# Revit family: 0039273 Feilo Sylvania Lighting Fixtures SYLBAY LED 4000K 18-5KLM WIDE 1-10V PIR
name_source: partatom
category: Lighting Fixtures
revit_build: Autodesk Revit 2017 (Build: 20190507_1515(x64)
units: mm (PartAtom-declared; Revit-internal decimal feet)

## family parameters
Cut with Voids When Loaded = No
Host = Face
Light Source = Yes
OmniClass Number = 23.80.70.00
OmniClass Title = Lighting
Part Type = Normal
Room Calculation Point = No
Round Connector Dimension = Use Diameter
Shared = No

## types (1)
- 0039273 SYLBAY LED 4000K 18.5KLM WIDE 1-10V PIR
    AccessoryMaterial = Accesory-Sylvania-Sylbay-White
    Apparent Load = 145 VA
    Assembly Code = D5020200
    AssetType = Fixed
    BodyMaterial = Body-Sylvania-Sylbay-Aluminium
    Color Filter = 16777215
    Cost = 0 $
    Default Elevation = 1219 mm
    Description = Specification industrial high bay luminaire, robust and durable, slim design, high output and efficiency, lightweight, aluminium housing with shatter-resistant polycarbonate lens optic, 18,800 lumens, 145W, 130lm/W, 4000K, 2100mA, CRI 80, wide beam optic, 1-10V dimmable, integral PIR sensor with daylight/occupancy detection, IP65, IK08, 100,000 hrs (L90B10), (LxWxH) 330x375x105mm, 3 step MacAdam ellipse, 4.6kg, aluminium finish, Class 1, 220-240V, integrated LED, energy class: A++, A+, A.
    DiffuserMaterial = Diffuser-Sylvania-Sylbay-Transparent
    Dimming Lamp Color Temperature Shift = <None>
    DimmingControlOptions = Dimmable
    DocumentationLiterature = http://www.sylvania-lighting.com
    DurationUnit = hours
    ElectricShockClassification = Class I
    Emit Shape Visible in Rendering = No
    Emit from Rectangle Length = 320 mm
    Emit from Rectangle Width = 365 mm
    ExpectedLife = 50000
    IfcExportAs = IfcLightFixtureType
    IfcExportType = IfcLightFixtureType
    ImpactProtectionIndex = IK08
    IngressProtection = IP65
    InputNominalFrequency = 50/60 Hz
    InputVoltage = 220-240V~
    Keynote = 16500
    Lamp = LED
    LampColourRenderingIndex = 80
    LampColourTemperature = 4000 K
    LampNominalLuminous = 18817 lm
    LampsType = LED
    LightOutputRatio = 100
    LuminousEfficacy = 130.67 lm/W
    Manufacturer = Feilo Sylvania
    ManufacturerName = Feilo Sylvania
    Material = aluminium housing
    Model = SYLBAY LED 4000K 18.5KLM WIDE 1-10V PIR
    ModelNumber = 0039273
    ModelReference = SYLBAY LED 4000K 18.5KLM WIDE 1-10V PIR
    Name = SYLBAY LED 4000K 18.5KLM WIDE 1-10V PIR
    NominalDepth = 375 mm  [stored 1.23031 ft]
    NominalHeight = 105 mm
    NominalLength = 430 mm
    Photometric Web File = 0039273.ies
    PowerConsumption = 145 W
    PowerFactor = 0
    ReflectorMaterial = <By Category>
    Tilt Angle = -90.00°
    Type Image = <None>
    TypeName = SYLBAY LED 4000K 18.5KLM WIDE 1-10V PIR
    URL = http://www.sylvania-lighting.com
    Voltage = 230 V
    Weight = 5.1 kg
    WireRadius_FEILO = 1 mm  [stored 0.00328084 ft]

note: [stored X ft] marks values corroborated as IEEE doubles in the binary element streams (Revit-internal decimal feet)

## geometry (parser evidence)
native form markers: Extrusion x6, Sweep x3
no freeform markers — native parametric forms only
